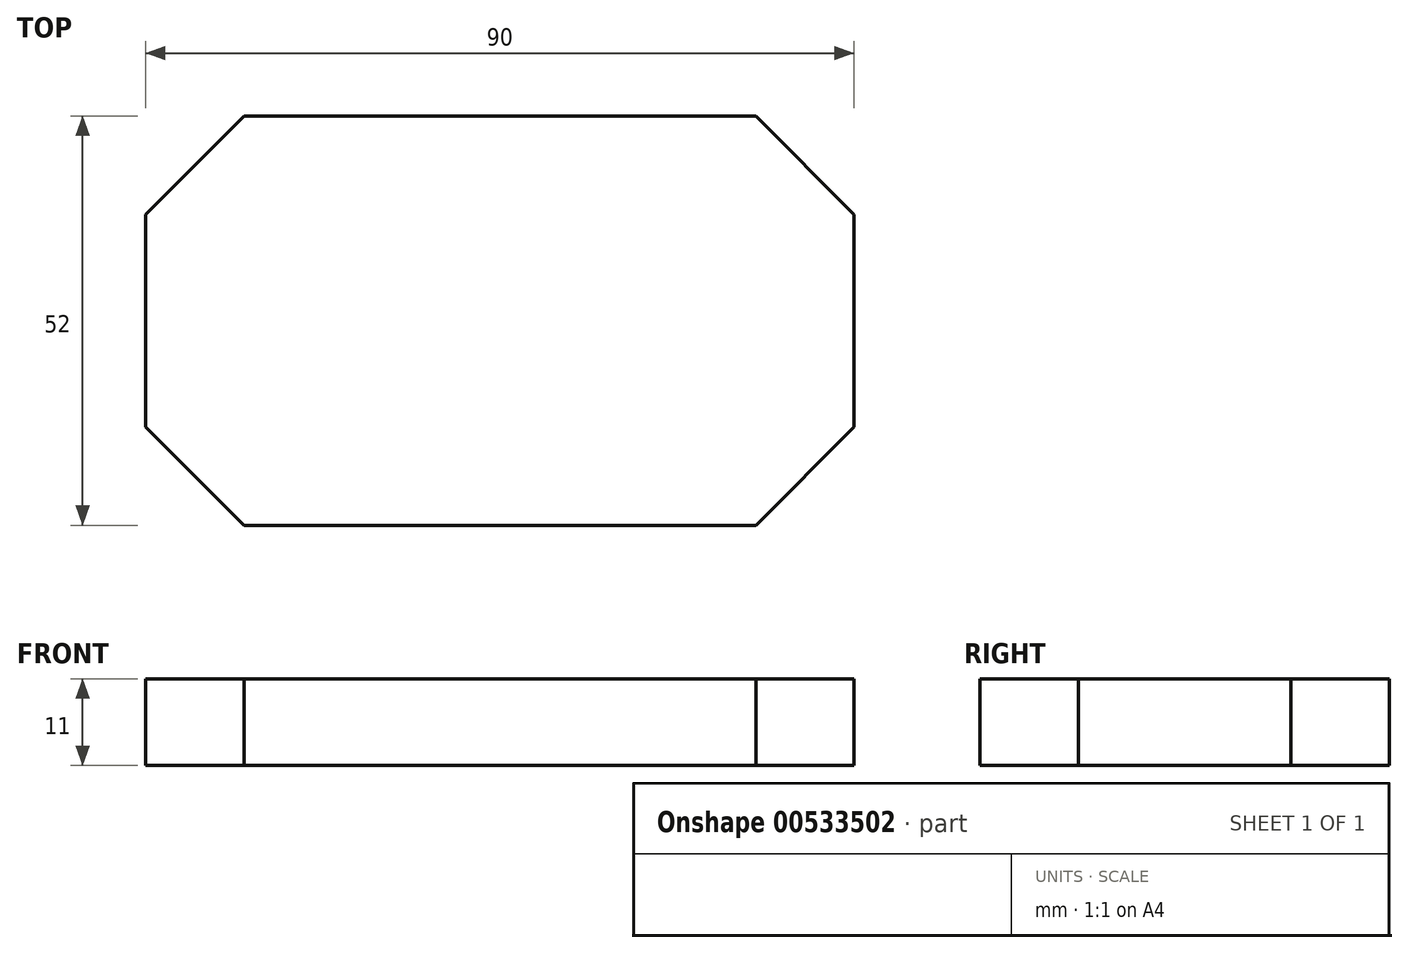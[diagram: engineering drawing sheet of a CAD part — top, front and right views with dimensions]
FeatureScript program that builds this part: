
annotation { "Feature Type Name" : "Feature", "Feature Type Description" : "" }
export const myFeature = defineFeature(function(context is Context, id is Id, definition is map)
    precondition{}
    {
        {
            var Q0;
            Q0=qCreatedBy(makeId("Top.planeOp"),FACE);
            var sketch = newSketch(context, id + "F0", { "sketchPlane" : qUnion([Q0])});
            skLineSegment(sketch, "E0.bottom", {"start": v(0, 0) * mm, "end": v(90, 0) * mm});
            skLineSegment(sketch, "E0.top", {"start": v(0, 52) * mm, "end": v(90, 52) * mm});
            skLineSegment(sketch, "E0.left", {"start": v(0, 0) * mm, "end": v(0, 52) * mm});
            skLineSegment(sketch, "E0.right", {"start": v(90, 0) * mm, "end": v(90, 52) * mm});
            skSolve(sketch);
        }
        {
            var Q0;
            Q0=qSketchRegion(id+"F0",true);
            extrude(context, id + "F1", {"entities" : qUnion([Q0]), "depth" : 11 * mm, "offsetDistance" : 25 * mm});
        }
        {
            var Q0;
            Q0=makeQuery(id+"F1.opExtrude","SWEPT_EDGE",EDGE,{"disambiguationData":[OSD([sQuery(id+"F0.wireOp",EDGE,"E0.bottom"),sQuery(id+"F0.wireOp",EDGE,"E0.left")])]});
            var Q1;
            Q1=makeQuery(id+"F1.opExtrude","SWEPT_EDGE",EDGE,{"disambiguationData":[OSD([sQuery(id+"F0.wireOp",EDGE,"E0.bottom"),sQuery(id+"F0.wireOp",EDGE,"E0.right")])]});
            var Q2;
            Q2=makeQuery(id+"F1.opExtrude","SWEPT_EDGE",EDGE,{"disambiguationData":[OSD([sQuery(id+"F0.wireOp",EDGE,"E0.top"),sQuery(id+"F0.wireOp",EDGE,"E0.right")])]});
            var Q3;
            Q3=makeQuery(id+"F1.opExtrude","SWEPT_EDGE",EDGE,{"disambiguationData":[OSD([sQuery(id+"F0.wireOp",EDGE,"E0.top"),sQuery(id+"F0.wireOp",EDGE,"E0.left")])]});
            chamfer(context, id + "F2", {"entities" : qUnion([Q0, Q1, Q2, Q3]), "width" : 12.5 * mm, "tangentPropagation" : true});
        }
    });
